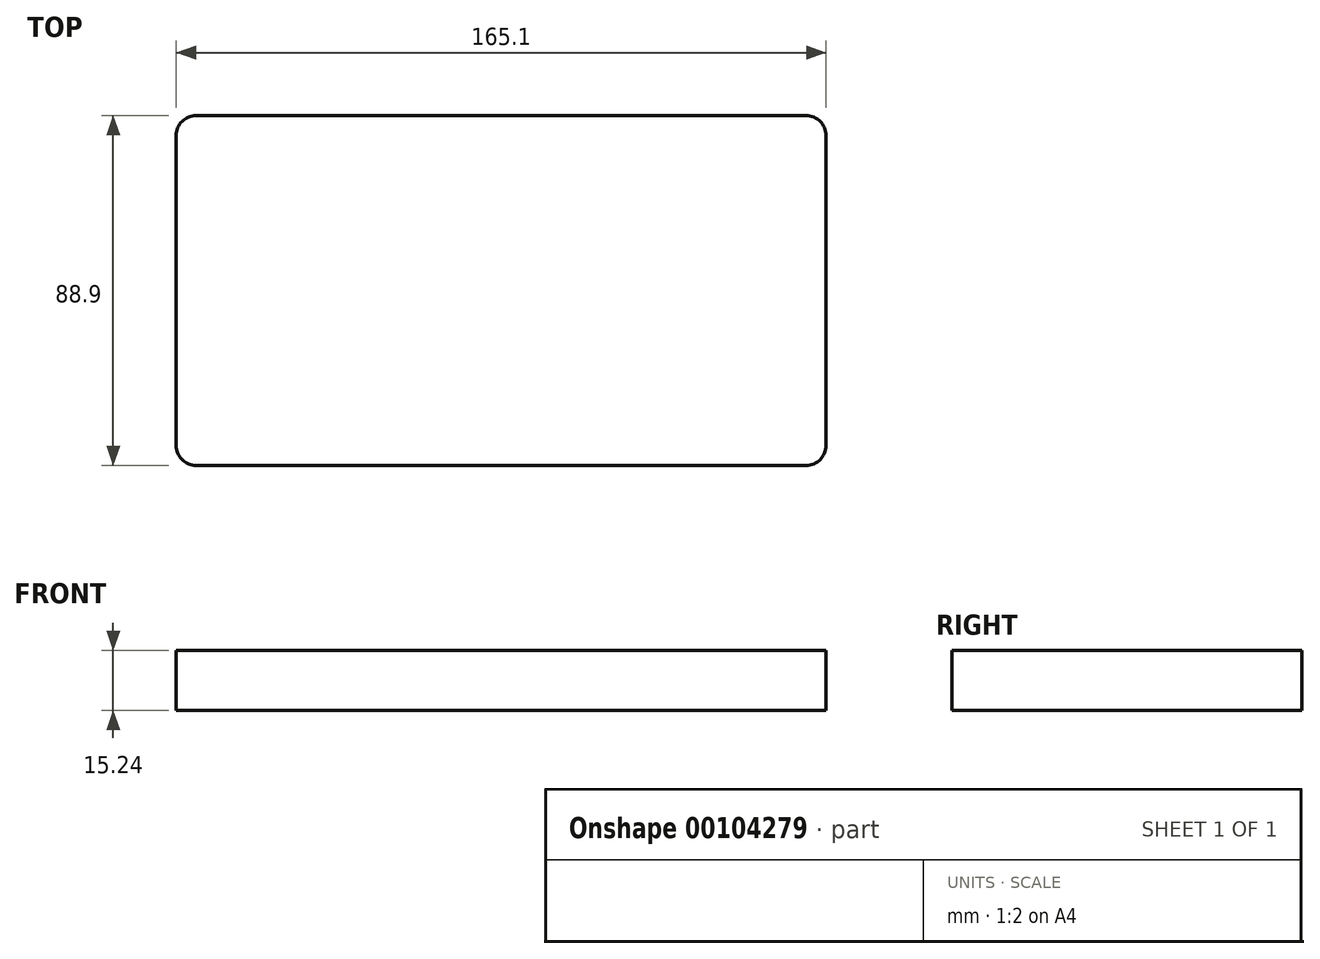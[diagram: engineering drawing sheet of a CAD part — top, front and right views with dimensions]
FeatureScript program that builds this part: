
annotation { "Feature Type Name" : "Feature", "Feature Type Description" : "" }
export const myFeature = defineFeature(function(context is Context, id is Id, definition is map)
    precondition{}
    {
        {
            var Q0;
            Q0=qCreatedBy(makeId("Top.planeOp"),FACE);
            var sketch = newSketch(context, id + "F0", { "sketchPlane" : qUnion([Q0])});
            skLineSegment(sketch, "E0.bottom", {"start": v(-86.77, 50.8) * mm, "end": v(78.33, 50.8) * mm});
            skLineSegment(sketch, "E0.top", {"start": v(-86.77, -38.1) * mm, "end": v(78.33, -38.1) * mm});
            skLineSegment(sketch, "E0.left", {"start": v(-86.77, 50.8) * mm, "end": v(-86.77, -38.1) * mm});
            skLineSegment(sketch, "E0.right", {"start": v(78.33, 50.8) * mm, "end": v(78.33, -38.1) * mm});
            skSolve(sketch);
        }
        {
            var Q0;
            Q0=makeQuery(id+"F0.imprint","IMPRINT",FACE,{"disambiguationData":[TD([[makeQuery(id+"F0.imprint","IMPRINT",EDGE,{"derivedFrom":sQuery(id+"F0.wireOp",EDGE,"E0.bottom")}),-1.0]])]});
            extrude(context, id + "F1", {"entities" : qUnion([Q0]), "depth" : 15.24 * mm});
        }
        {
            var Q0;
            Q0=makeQuery(id+"F1.opExtrude","SWEPT_EDGE",EDGE,{"disambiguationData":[OSD([sQuery(id+"F0.wireOp",EDGE,"E0.top"),sQuery(id+"F0.wireOp",EDGE,"E0.left")])]});
            fillet(context, id + "F2", {"entities" : qUnion([Q0]), "radius" : 5.08 * mm, "tangentPropagation" : true, "allowEdgeOverflow" : false});
        }
        {
            var Q0;
            Q0=makeQuery(id+"F1.opExtrude","SWEPT_EDGE",EDGE,{"disambiguationData":[OSD([sQuery(id+"F0.wireOp",EDGE,"E0.top"),sQuery(id+"F0.wireOp",EDGE,"E0.right")])]});
            fillet(context, id + "F3", {"entities" : qUnion([Q0]), "radius" : 5.08 * mm, "tangentPropagation" : true, "allowEdgeOverflow" : false});
        }
        {
            var Q0;
            Q0=makeQuery(id+"F1.opExtrude","SWEPT_EDGE",EDGE,{"disambiguationData":[OSD([sQuery(id+"F0.wireOp",EDGE,"E0.bottom"),sQuery(id+"F0.wireOp",EDGE,"E0.right")])]});
            fillet(context, id + "F4", {"entities" : qUnion([Q0]), "radius" : 5.08 * mm, "tangentPropagation" : true, "allowEdgeOverflow" : false});
        }
        {
            var Q0;
            Q0=makeQuery(id+"F1.opExtrude","SWEPT_EDGE",EDGE,{"disambiguationData":[OSD([sQuery(id+"F0.wireOp",EDGE,"E0.bottom"),sQuery(id+"F0.wireOp",EDGE,"E0.left")])]});
            fillet(context, id + "F5", {"entities" : qUnion([Q0]), "radius" : 5.08 * mm, "tangentPropagation" : true, "allowEdgeOverflow" : false});
        }
    });
